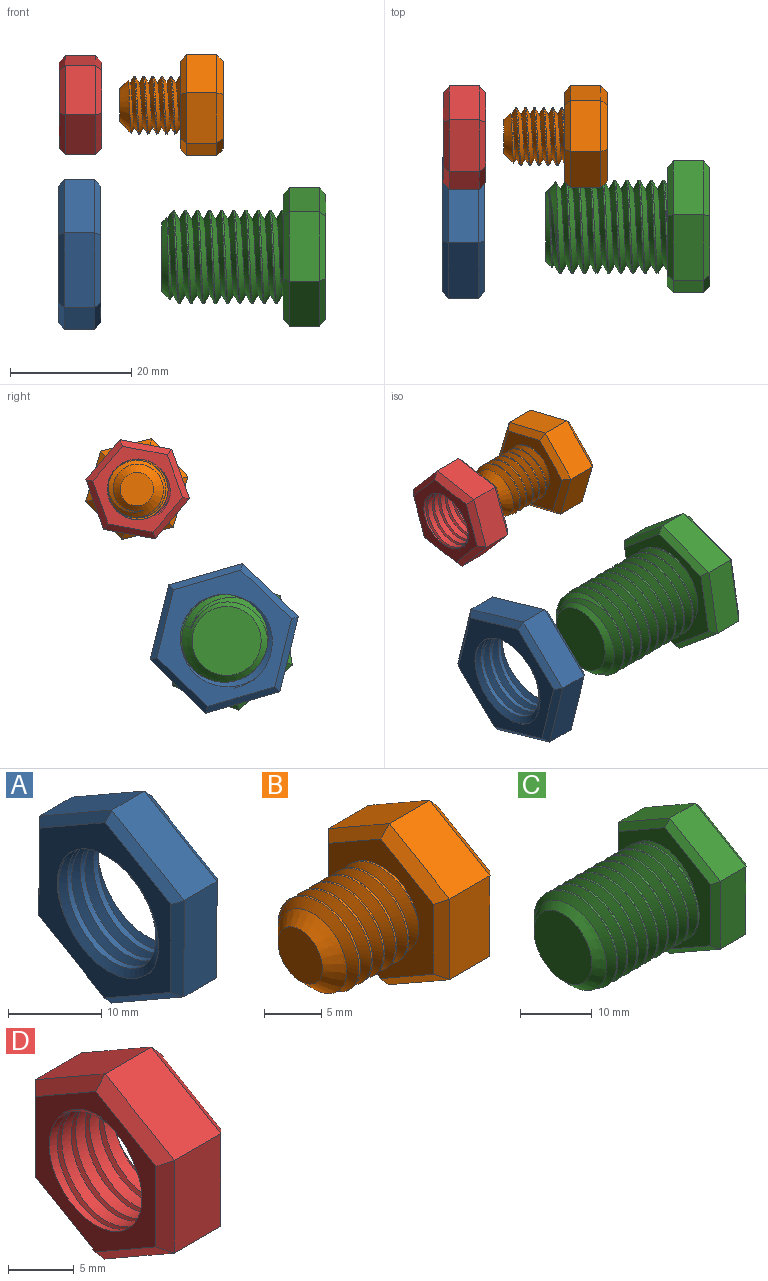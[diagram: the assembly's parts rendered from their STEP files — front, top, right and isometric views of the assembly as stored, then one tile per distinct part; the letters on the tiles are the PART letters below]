
ASSEMBLY  parts=4 mates=2
PART A: 23 faces, bbox 9.3x22.7x26 mm
  f0: cylinder r=7.24mm len=14.48mm, axis (1,0,0), area 111.6mm2, adj f7,f8,f21,f22
  f1: plane 10.98x6.38mm, normal (0,-0.5,0.86), area 63.5mm2, adj f2,f6,f14,f18
  f2: plane 12.7x5mm, normal (0,-1,0), area 63.5mm2, adj f1,f3,f12,f16
  f3: plane 11.02x6.32mm, normal (0,-0.5,-0.87), area 63.5mm2, adj f2,f4,f10,f15
  f4: plane 10.98x6.38mm, normal (0,0.5,-0.86), area 63.5mm2, adj f3,f5,f9,f17
  f5: plane 12.7x5mm, normal (0,1,0), area 63.5mm2, adj f4,f6,f11,f19
  f6: plane 11.02x6.32mm, normal (0,0.5,0.87), area 63.5mm2, adj f1,f5,f13,f20
  f7: plane 23.73x20.67mm, normal (-1,0,0), area 164.4mm2, adj f0,f9,f10,f11,f12,f13,f14,f21
  f8: plane 23.73x20.67mm, normal (1,0,0), area 164.4mm2, adj f0,f15,f16,f17,f18,f19,f20,f21
  f9: plane 10.99x6.96mm, normal (-0.71,0.36,-0.61), area 17.1mm2, adj f4,f7,f10,f11
  f10: plane 11.02x6.9mm, normal (-0.71,-0.35,-0.61), area 17.1mm2, adj f3,f7,f9,f12
  f11: plane 12.7x1.03mm, normal (-0.71,0.71,0), area 17.1mm2, adj f5,f7,f9,f13
  f12: plane 12.7x1.03mm, normal (-0.71,-0.71,0), area 17.1mm2, adj f2,f7,f10,f14
  f13: plane 11.02x6.9mm, normal (-0.71,0.35,0.61), area 17.1mm2, adj f6,f7,f11,f14
  f14: plane 10.99x6.96mm, normal (-0.71,-0.36,0.61), area 17.1mm2, adj f1,f7,f12,f13
  f15: plane 11.02x6.9mm, normal (0.71,-0.35,-0.61), area 17.1mm2, adj f3,f8,f16,f17
  f16: plane 12.7x1.03mm, normal (0.71,-0.71,0), area 17.1mm2, adj f2,f8,f15,f18
  f17: plane 10.99x6.96mm, normal (0.71,0.36,-0.61), area 17.1mm2, adj f4,f8,f15,f19
  f18: plane 10.99x6.96mm, normal (0.71,-0.36,0.61), area 17.1mm2, adj f1,f8,f16,f20
  f19: plane 12.7x1.03mm, normal (0.71,0.71,0), area 17.1mm2, adj f5,f8,f17,f20
  f20: plane 11.02x6.9mm, normal (0.71,0.35,0.61), area 17.1mm2, adj f6,f8,f18,f19
  f21: bspline ~19.31x16.73mm, area 223mm2, adj f0,f7,f8,f22
  f22: bspline ~19.31x16.73mm, area 223mm2, adj f0,f7,f8,f21
PART B: 25 faces, bbox 17.8x15.9x18.1 mm
  f0: cylinder r=4.75mm len=9.5mm, axis (1,0,0), area 28.1mm2, adj f1,f2,f4,f12
  f1: bspline ~10.97x9.91mm, area 196.7mm2, adj f0,f2,f4,f12
  f2: bspline ~10.97x10.66mm, area 196.6mm2, adj f0,f1,f4,f12
  f3: plane 5.5x5.5mm, normal (-1,0,0), area 23.8mm2, adj f4
  f4: cone r=4.75mm half-angle=45deg, axis (1,0,0), area 47.4mm2, adj f0,f1,f2,f3
  f5: plane 7.48x5mm, normal (0,-0.5,0.86), area 43.3mm2, adj f6,f10,f18,f22
  f6: plane 8.66x5mm, normal (0,-1,0), area 43.3mm2, adj f5,f7,f16,f20
  f7: plane 7.52x5mm, normal (0,-0.5,-0.87), area 43.3mm2, adj f6,f8,f14,f19
  f8: plane 7.48x5mm, normal (0,0.5,-0.86), area 43.3mm2, adj f7,f9,f13,f21
  f9: plane 8.66x5mm, normal (0,1,0), area 43.3mm2, adj f8,f10,f15,f23
  f10: plane 7.52x5mm, normal (0,0.5,0.87), area 43.3mm2, adj f5,f9,f17,f24
  f11: plane 15.01x13.03mm, normal (1,0,0), area 146.4mm2, adj f13,f14,f15,f16,f17,f18
  f12: plane 15.83x13.85mm, normal (-1,0,0), area 89.2mm2, adj f0,f1,f2,f19,f20,f21,f22,f23
  f13: plane 7.49x4.93mm, normal (0.71,0.36,-0.61), area 11.4mm2, adj f8,f11,f14,f15
  f14: plane 7.52x4.88mm, normal (0.71,-0.35,-0.61), area 11.4mm2, adj f7,f11,f13,f16
  f15: plane 8.66x1.03mm, normal (0.71,0.71,0), area 11.4mm2, adj f9,f11,f13,f17
  f16: plane 8.66x1.03mm, normal (0.71,-0.71,0), area 11.4mm2, adj f6,f11,f14,f18
  f17: plane 7.52x4.88mm, normal (0.71,0.35,0.61), area 11.4mm2, adj f10,f11,f15,f18
  f18: plane 7.49x4.93mm, normal (0.71,-0.36,0.61), area 11.4mm2, adj f5,f11,f16,f17
  f19: plane 7.52x4.88mm, normal (-0.71,-0.35,-0.61), area 11.4mm2, adj f7,f12,f20,f21
  f20: plane 8.66x1.03mm, normal (-0.71,-0.71,0), area 11.4mm2, adj f6,f12,f19,f22
  f21: plane 7.49x4.93mm, normal (-0.71,0.36,-0.61), area 11.4mm2, adj f8,f12,f19,f23
  f22: plane 7.49x4.93mm, normal (-0.71,-0.36,0.61), area 11.4mm2, adj f5,f12,f20,f24
  f23: plane 8.66x1.03mm, normal (-0.71,0.71,0), area 11.4mm2, adj f9,f12,f21,f24
  f24: plane 7.52x4.88mm, normal (-0.71,0.35,0.61), area 11.4mm2, adj f10,f12,f22,f23
PART C: 26 faces, bbox 27.7x20x23.1 mm
  f0: cylinder r=7.68mm len=18mm, axis (1,0,0), area 139.1mm2, adj f1,f2,f5,f13
  f1: bspline ~20.88x17.74mm, area 713.8mm2, adj f0,f2,f4,f5,f13
  f2: bspline ~21.88x17.74mm, area 715.1mm2, adj f0,f1,f4,f5,f13
  f3: plane 11.36x11.36mm, normal (-1,0,0), area 101.4mm2, adj f4
  f4: cone r=7.68mm half-angle=45deg, axis (1,0,0), area 63.2mm2, adj f1,f2,f3,f5
  f5: cone r=7.68mm half-angle=45deg, axis (1,0,0), area 13.2mm2, adj f0,f1,f2,f4
  f6: plane 9.98x5.81mm, normal (0,-0.5,0.86), area 57.7mm2, adj f7,f11,f19,f23
  f7: plane 11.55x5mm, normal (0,-1,0), area 57.7mm2, adj f6,f8,f17,f21
  f8: plane 10.02x5.74mm, normal (0,-0.5,-0.87), area 57.7mm2, adj f7,f9,f15,f20
  f9: plane 9.98x5.81mm, normal (0,0.5,-0.86), area 57.7mm2, adj f8,f10,f14,f22
  f10: plane 11.55x5mm, normal (0,1,0), area 57.7mm2, adj f9,f11,f16,f24
  f11: plane 10.02x5.74mm, normal (0,0.5,0.87), area 57.7mm2, adj f6,f10,f18,f25
  f12: plane 20.78x18.04mm, normal (1,0,0), area 280.6mm2, adj f14,f15,f16,f17,f18,f19
  f13: plane 20.78x18.04mm, normal (-1,0,0), area 125.2mm2, adj f0,f1,f2,f20,f21,f22,f23,f24
  f14: plane 9.98x6.38mm, normal (0.71,0.36,-0.61), area 15.5mm2, adj f9,f12,f15,f16
  f15: plane 10.02x6.32mm, normal (0.71,-0.35,-0.61), area 15.5mm2, adj f8,f12,f14,f17
  f16: plane 11.55x1.04mm, normal (0.71,0.71,0), area 15.5mm2, adj f10,f12,f14,f18
  f17: plane 11.55x1.04mm, normal (0.71,-0.71,0), area 15.5mm2, adj f7,f12,f15,f19
  f18: plane 10.02x6.32mm, normal (0.71,0.35,0.61), area 15.5mm2, adj f11,f12,f16,f19
  f19: plane 9.98x6.38mm, normal (0.71,-0.36,0.61), area 15.5mm2, adj f6,f12,f17,f18
  f20: plane 10.02x6.32mm, normal (-0.71,-0.35,-0.61), area 15.5mm2, adj f8,f13,f21,f22
  f21: plane 11.55x1.04mm, normal (-0.71,-0.71,0), area 15.5mm2, adj f7,f13,f20,f23
  f22: plane 9.98x6.38mm, normal (-0.71,0.36,-0.61), area 15.5mm2, adj f9,f13,f20,f24
  f23: plane 9.98x6.38mm, normal (-0.71,-0.36,0.61), area 15.5mm2, adj f6,f13,f21,f25
  f24: plane 11.55x1.04mm, normal (-0.71,0.71,0), area 15.5mm2, adj f10,f13,f22,f25
  f25: plane 10.02x6.32mm, normal (-0.71,0.35,0.61), area 15.5mm2, adj f11,f13,f23,f24
PART D: 23 faces, bbox 8.8x15x17.3 mm
  f0: cylinder r=5mm len=10mm, axis (1,0,0), area 150mm2, adj f7,f8,f21,f22
  f1: plane 7.49x5mm, normal (0,-0.5,0.86), area 43.3mm2, adj f2,f6,f14,f18
  f2: plane 8.66x5mm, normal (0,-1,0), area 43.3mm2, adj f1,f3,f12,f16
  f3: plane 7.51x5mm, normal (0,-0.5,-0.87), area 43.3mm2, adj f2,f4,f10,f15
  f4: plane 7.49x5mm, normal (0,0.5,-0.86), area 43.3mm2, adj f3,f5,f9,f17
  f5: plane 8.66x5mm, normal (0,1,0), area 43.3mm2, adj f4,f6,f11,f19
  f6: plane 7.51x5mm, normal (0,0.5,0.87), area 43.3mm2, adj f1,f5,f13,f20
  f7: plane 15.01x13.02mm, normal (-1,0,0), area 65.7mm2, adj f0,f9,f10,f11,f12,f13,f14,f21
  f8: plane 15.01x13.02mm, normal (1,0,0), area 65.7mm2, adj f0,f15,f16,f17,f18,f19,f20,f21
  f9: plane 7.49x4.93mm, normal (-0.71,0.36,-0.61), area 11.4mm2, adj f4,f7,f10,f11
  f10: plane 7.51x4.89mm, normal (-0.71,-0.35,-0.61), area 11.4mm2, adj f3,f7,f9,f12
  f11: plane 8.66x1.02mm, normal (-0.71,0.71,0), area 11.4mm2, adj f5,f7,f9,f13
  f12: plane 8.66x1.02mm, normal (-0.71,-0.71,0), area 11.4mm2, adj f2,f7,f10,f14
  f13: plane 7.51x4.89mm, normal (-0.71,0.35,0.61), area 11.4mm2, adj f6,f7,f11,f14
  f14: plane 7.49x4.93mm, normal (-0.71,-0.36,0.61), area 11.4mm2, adj f1,f7,f12,f13
  f15: plane 7.51x4.89mm, normal (0.71,-0.35,-0.61), area 11.4mm2, adj f3,f8,f16,f17
  f16: plane 8.66x1.02mm, normal (0.71,-0.71,0), area 11.4mm2, adj f2,f8,f15,f18
  f17: plane 7.49x4.93mm, normal (0.71,0.36,-0.61), area 11.4mm2, adj f4,f8,f15,f19
  f18: plane 7.49x4.93mm, normal (0.71,-0.36,0.61), area 11.4mm2, adj f1,f8,f16,f20
  f19: plane 8.66x1.02mm, normal (0.71,0.71,0), area 11.4mm2, adj f5,f8,f17,f20
  f20: plane 7.51x4.89mm, normal (0.71,0.35,0.61), area 11.4mm2, adj f6,f8,f18,f19
  f21: bspline ~12.5x10.82mm, area 72.8mm2, adj f0,f7,f8,f22
  f22: bspline ~12.5x10.82mm, area 72.8mm2, adj f0,f7,f8,f21
PLACE A rot(axis=(0,0.6,-0.8),180deg) t=(-55.27,-6.86,23.48)mm fixed
PLACE B rot(axis=(-1,0,0),43.8deg) t=(-31.66,7.53,48.05)mm
PLACE C rot(axis=(1,0,0),109.9deg) t=(-14.77,-7.25,23.06)mm
PLACE D rot(axis=(1,0,0),100.2deg) t=(-48.16,7.38,48.02)mm fixed
MATE cylindrical C.f0 <-> A.f7  axis (-1,0,0) through (-38.27,-7.25,23.06)mm
MATE cylindrical B.f0 <-> D.f7  axis (-1,0,0) through (-45.16,7.53,48.05)mm
